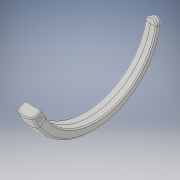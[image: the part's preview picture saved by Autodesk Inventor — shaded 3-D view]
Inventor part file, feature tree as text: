
AUTODESK INVENTOR PART (.ipt)
format: ipt  version: 2019 (Build 230136000, 136)  size: 680,448 bytes
history: native  units: mm
features: sketch x4, other x3, fillet x2, projected_geometry x2, plane x1, sweep x1, hole x1, revolve x1
ambient origin geometry x8: Origin, YZ Plane, XZ Plane, XY Plane, X Axis, Y Axis, Z Axis, Center Point
bodies: Body1 (feature_tree)
feature tree (15):
  other  "<userpath>\Desktop\3D Sketches\Bulova\Parameter.xlsx"
  other  "Foto"
  sketch  "Skizze15"  dims[d13=5.0mm d14=8.0mm d107=5.0mm d134=5.0mm]
  plane  "Arbeitsebene22"
  sweep  "Sweeping2"
  hole  "Bohrung1"  [1 undecoded]
  revolve  "Umdrehung1"
  fillet  "Rundung1"  [1 undecoded]
  fillet  "Rundung2"  Radius=1.5mm
  other  "Bild1"
  sketch  "Skizze16"  dims[d140=4.5mm d141=2.5mm d142=-0.174533mm d143=0.0mm]
  sketch  "Skizze17"  dims[d144=1.0mm d145=6.0mm d146=4.0mm d147=2.0mm d148=90.0deg d149=6.0mm d150=0.0mm d151=1.5mm]
  projected_geometry  "Projizierte Kontur2"
  sketch  "Skizze18"  dims[d152=3.0mm d153=180.0deg d154=16.5mm d155=0.5mm d156=0.3mm d157=0.3mm]
  projected_geometry  "Projizierte Kontur3"
note: 2 required parameter values undecoded (feature->parameter linkage not recoverable at this tier; creation-order binding heuristic only, values carry confidence <= 0.55)
